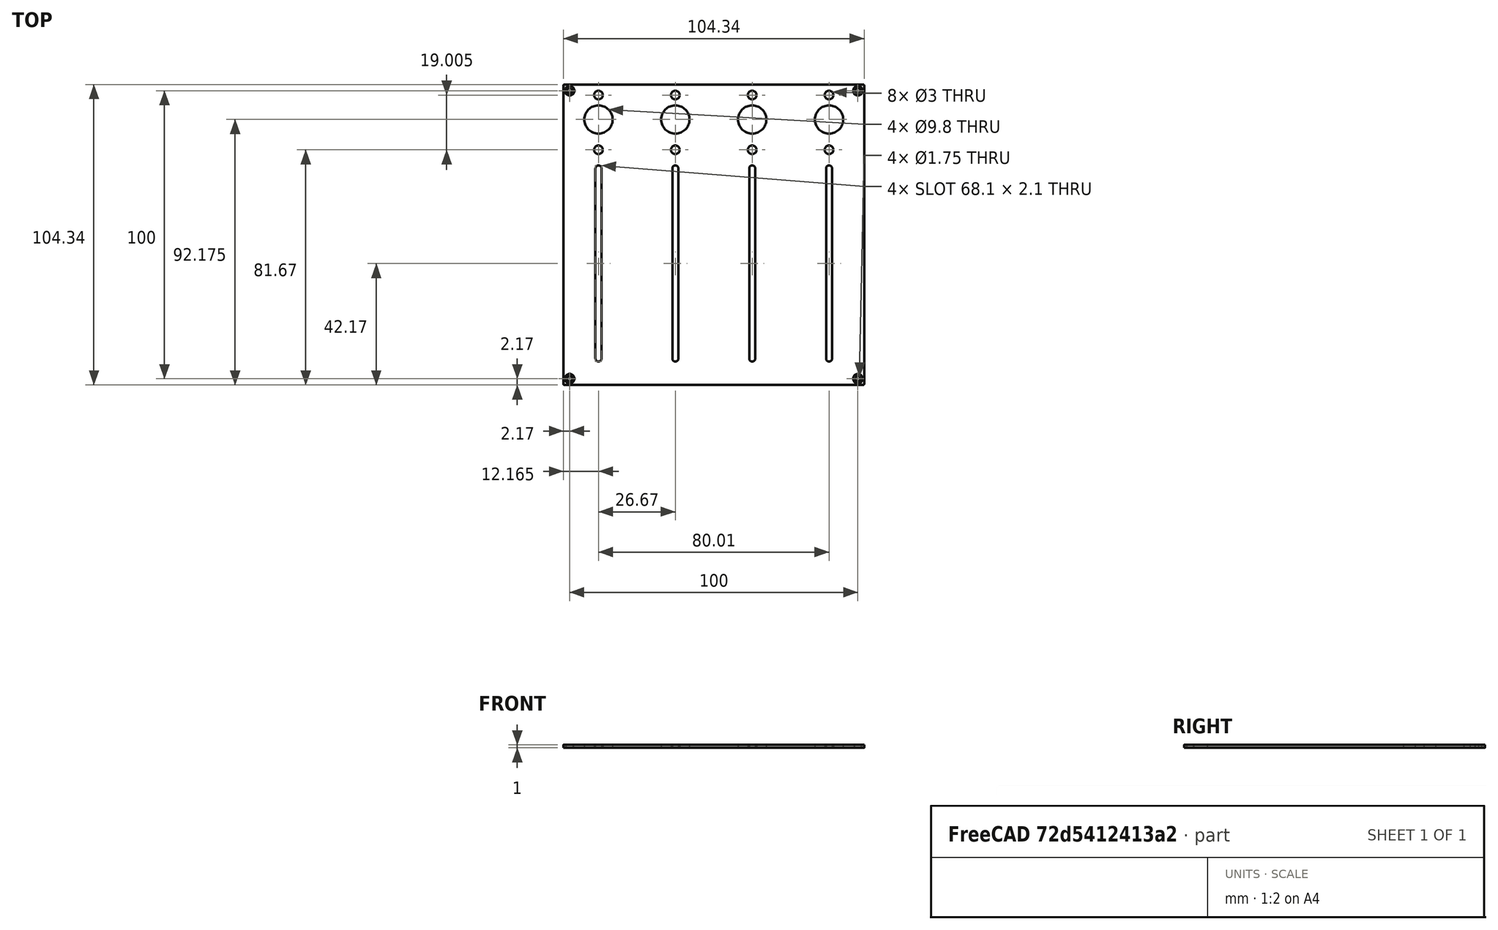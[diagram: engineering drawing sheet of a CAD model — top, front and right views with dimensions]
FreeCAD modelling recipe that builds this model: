
FCSTD DOCUMENT  (FreeCAD 0.21R33771 (Git))
Label: FRONTPANEL-SHEET-EF44
License: All rights reserved
LicenseURL: https://en.wikipedia.org/wiki/All_rights_reserved
objects: TechDraw::DrawViewBalloon×16, TechDraw::DrawViewDimension×8, Sketcher::SketchObject×7, TechDraw::DrawViewPart×5, TechDraw::DrawHatch×5, PartDesign::Hole×3, TechDraw::DrawViewAnnotation×3, TechDraw::DrawSVGTemplate×2, PartDesign::Pocket×2, PartDesign::Body×2, TechDraw::DrawPage×2, Spreadsheet::Sheet×1, PartDesign::Pad×1, PartDesign::FeatureBase×1, TechDraw::DrawComplexSection×1
note: 33 computed .brp shape members not serialized (recipe doc carries the construction recipe); baked Part::Feature solids carry a one-line shape summary decoded from their .brp

FEATURE [TechDraw::DrawSVGTemplate] Template
  EditableTexts = COLOR=Anodized matte black - RAL code: 9004; CreationDate=2024/05/14; E.G.APPROVED=APPROVED; FC-Scale=1:1; FC-Title=EF44 - frontpanel; IntechStudioLtd.=Intech Studio Ltd.; MATERIAL=Aluminum 5052-H32; REV=04; STANDARD=ISO 2768 - m
  Height = 297
  Orientation = 1
  Template = <userpath>/Desktop/A3_LandscapeTD_MODIFIED.svg
  Width = 420
FEATURE [Sketcher::SketchObject] Sketch022
  FullyConstrained = true
  MapMode = 5
  Support = -> [XY_Plane010]
  sketch-geometry (18):
    g0: Circle CenterX=-40.005 CenterY=48.505 CenterZ=0 NormalX=0 NormalY=0 NormalZ=1 AngleXU=0 Radius=2
    g1: Circle CenterX=-13.335 CenterY=48.505 CenterZ=0 NormalX=0 NormalY=0 NormalZ=1 AngleXU=0 Radius=2
    g2: Circle CenterX=13.335 CenterY=48.505 CenterZ=0 NormalX=0 NormalY=0 NormalZ=1 AngleXU=0 Radius=2
    g3: Circle CenterX=40.005 CenterY=48.505 CenterZ=0 NormalX=0 NormalY=0 NormalZ=1 AngleXU=0 Radius=2
    g4: Circle CenterX=-40.005 CenterY=29.5 CenterZ=0 NormalX=0 NormalY=0 NormalZ=1 AngleXU=0 Radius=2
    g5: Circle CenterX=-13.335 CenterY=29.5 CenterZ=0 NormalX=0 NormalY=0 NormalZ=1 AngleXU=0 Radius=2
    g6: Circle CenterX=13.335 CenterY=29.5 CenterZ=0 NormalX=0 NormalY=0 NormalZ=1 AngleXU=0 Radius=2
    g7: Circle CenterX=40.005 CenterY=29.5 CenterZ=0 NormalX=0 NormalY=0 NormalZ=1 AngleXU=0 Radius=2
    g8: LineSegment StartX=-40.005 StartY=48.505 StartZ=0 EndX=-13.335 EndY=48.505 EndZ=0
    g9: LineSegment StartX=13.335 StartY=48.505 StartZ=0 EndX=-13.335 EndY=48.505 EndZ=0
    g10: LineSegment StartX=13.335 StartY=48.505 StartZ=0 EndX=40.005 EndY=48.505 EndZ=0
    g11: LineSegment StartX=-40.005 StartY=29.5 StartZ=0 EndX=-13.335 EndY=29.5 EndZ=0
    g12: LineSegment StartX=-13.335 StartY=29.5 StartZ=0 EndX=13.335 EndY=29.5 EndZ=0
    g13: LineSegment StartX=13.335 StartY=29.5 StartZ=0 EndX=40.005 EndY=29.5 EndZ=0
    g14: LineSegment StartX=-13.335 StartY=48.505 StartZ=0 EndX=0 EndY=8.5 EndZ=0
    g15: LineSegment StartX=0 StartY=8.5 StartZ=0 EndX=13.335 EndY=48.505 EndZ=0
    g16: LineSegment StartX=-13.335 StartY=29.5 StartZ=0 EndX=0 EndY=0 EndZ=0
    g17: LineSegment StartX=0 StartY=0 StartZ=0 EndX=13.335 EndY=29.5 EndZ=0
  constraints (45):
    c: Diameter(g7) = 4
    c: Equal(g7,g6)
    c: Equal(g7,g2)
    c: Equal(g7,g3)
    c: Equal(g7,g1)
    c: Equal(g7,g5)
    c: Equal(g7,g4)
    c: Equal(g7,g0)
    c: Coincident(g8,g0)
    c: Coincident(g8,g1)
    c: Horizontal(g8)
    c: Coincident(g9,g2)
    c: Coincident(g9,g1)
    c: Horizontal(g9)
    c: Coincident(g10,g2)
    c: Coincident(g10,g3)
    c: Horizontal(g10)
    c: Coincident(g11,g4)
    c: Coincident(g11,g5)
    c: Coincident(g12,g5)
    c: Coincident(g12,g6)
    c: Horizontal(g12)
    c: Coincident(g13,g6)
    c: Coincident(g13,g7)
    c: Horizontal(g13)
    c: Horizontal(g11)
    c: Equal(g11,g12)
    c: Equal(g12,g13)
    c: Equal(g13,g10)
    c: Equal(g10,g9)
    c: Equal(g9,g8)
    c: Coincident(g14,g1)
    c: PointOnObject(g14,g-2)
    c: Coincident(g14,g15)
    c: Coincident(g15,g2)
    c: Equal(g14,g15)
    c: DistanceX(g8,g8) = 26.67
    c: DistanceY(g-1,g14) = 8.5
    c: DistanceY(g14,g1) = 40.005
    c: DistanceY(g-1,g5) = 29.5
    c: Coincident(g16,g5)
    c: Coincident(g16,g-1)
    c: Coincident(g16,g17)
    c: Coincident(g17,g6)
    c: Equal(g17,g16)
FEATURE [Spreadsheet::Sheet] Spreadsheet  label="dim"
  cells = A1='panel_length; B1(panel_length)=104.35; A2='panel_thickness; B2(panel_thickness)=1; A3='panel_radius; B3(panel_radius)==(104.35 - 103.6) / 2; A5='corner_drill_dist; B5(corner_drill_dist)=100; A6='corner_drill_dia; B6(corner_drill_dia)=1.75; A7='corner_drill_countersink; B7(corner_drill_countersink)=3.3; A9='undercut_width; B9(undercut_width)=1; A10='undercut_length; B10(undercut_length)=90; A11='undercut_offset; B11(undercut_offset)=1; A12='undercut_depth; B12(undercut_depth)=0.8; A14='ui_raster; B14(ui_raster)=26.67; A16='light_drill_dia; B16(light_drill_dia)=3; D16='old 2.9; A17='light_bore_dia; B17(light_bore_dia)=3.45; C17='check; D17='old 3.30; E17='DEPRICATED; A18='light_bore_depth; B18(light_bore_depth)=0.4; C18='check; D18='old 0.40; E18='DEPRICATED; A20='pot_drill_dia; B20(pot_drill_dia)=9.8; C20='check; D20='old 6.20; A21='pot_led_dist; B21(pot_led_dist)=8.5; B22=0; A23='but_drill_dia; B23(but_drill_dia)=9.8; A24='but_led_dist; B24(but_led_dist)=8.5; A26='fad_cutout_width; B26(fad_cutout_width)=2.1; C26='check; D26='old 1.50; A27='fad_cutout_length; B27(fad_cutout_length)=36; A28='fad_led_dist; B28(fad_led_dist)=25; A30='enc_drill_dia; B30(enc_drill_dia)=9.8; C30='check; D30='old 6.20; A31='enc_led_dist; B31(enc_led_dist)=8.5; A33='longfad_cutout_width; B33(longfad_cutout_width)=2.1; A34='longfad_cutout_length; B34(longfad_cutout_length)=66; A36='panel_chamfer; B36(panel_chamfer)=0.2; C36='UPDATE DRAWING
FEATURE [Sketcher::SketchObject] Sketch021
  FullyConstrained = true
  MapMode = 5
  Support = -> [XY_Plane010]
  expr: Constraints[48] = <<dim>>.longfad_cutout_length
  expr: Constraints[49] = <<dim>>.longfad_cutout_width
  sketch-geometry (25):
    g0: ArcOfCircle CenterX=-40.005 CenterY=23 CenterZ=0 NormalX=0 NormalY=0 NormalZ=1 AngleXU=0 Radius=1.05 StartAngle=-6.8008e-12 EndAngle=3.14159
    g1: ArcOfCircle CenterX=-40.005 CenterY=-43 CenterZ=0 NormalX=0 NormalY=0 NormalZ=1 AngleXU=0 Radius=1.05 StartAngle=3.14159 EndAngle=6.28319
    g2: LineSegment StartX=-41.055 StartY=23 StartZ=0 EndX=-41.055 EndY=-43 EndZ=0
    g3: LineSegment StartX=-38.955 StartY=23 StartZ=0 EndX=-38.955 EndY=-43 EndZ=0
    g4: ArcOfCircle CenterX=-13.335 CenterY=23 CenterZ=0 NormalX=0 NormalY=0 NormalZ=1 AngleXU=0 Radius=1.05 StartAngle=-1.8e-15 EndAngle=3.14159
    g5: ArcOfCircle CenterX=-13.335 CenterY=-43 CenterZ=0 NormalX=0 NormalY=0 NormalZ=1 AngleXU=0 Radius=1.05 StartAngle=3.14159 EndAngle=6.28319
    g6: LineSegment StartX=-14.385 StartY=23 StartZ=0 EndX=-14.385 EndY=-43 EndZ=0
    g7: LineSegment StartX=-12.285 StartY=23 StartZ=0 EndX=-12.285 EndY=-43 EndZ=0
    g8: ArcOfCircle CenterX=13.335 CenterY=23 CenterZ=0 NormalX=0 NormalY=0 NormalZ=1 AngleXU=0 Radius=1.05 StartAngle=-9e-16 EndAngle=3.14159
    g9: ArcOfCircle CenterX=13.335 CenterY=-43 CenterZ=0 NormalX=0 NormalY=0 NormalZ=1 AngleXU=0 Radius=1.05 StartAngle=3.14159 EndAngle=6.28319
    g10: LineSegment StartX=12.285 StartY=23 StartZ=0 EndX=12.285 EndY=-43 EndZ=0
    g11: LineSegment StartX=14.385 StartY=23 StartZ=0 EndX=14.385 EndY=-43 EndZ=0
    g12: ArcOfCircle CenterX=40.005 CenterY=23 CenterZ=0 NormalX=0 NormalY=0 NormalZ=1 AngleXU=0 Radius=1.05 StartAngle=-9e-16 EndAngle=3.14159
    g13: ArcOfCircle CenterX=40.005 CenterY=-43 CenterZ=0 NormalX=0 NormalY=0 NormalZ=1 AngleXU=0 Radius=1.05 StartAngle=3.14159 EndAngle=6.28319
    g14: LineSegment StartX=38.955 StartY=23 StartZ=0 EndX=38.955 EndY=-43 EndZ=0
    g15: LineSegment StartX=41.055 StartY=23 StartZ=0 EndX=41.055 EndY=-43 EndZ=0
    g16: LineSegment StartX=-40.005 StartY=23 StartZ=0 EndX=-13.335 EndY=23 EndZ=0
    g17: LineSegment StartX=-13.335 StartY=23 StartZ=0 EndX=13.335 EndY=23 EndZ=0
    g18: LineSegment StartX=13.335 StartY=23 StartZ=0 EndX=40.005 EndY=23 EndZ=0
    g19: LineSegment StartX=-40.005 StartY=-43 StartZ=0 EndX=-13.335 EndY=-43 EndZ=0
    g20: LineSegment StartX=-13.335 StartY=-43 StartZ=0 EndX=13.335 EndY=-43 EndZ=0
    g21: LineSegment StartX=13.335 StartY=-43 StartZ=0 EndX=40.005 EndY=-43 EndZ=0
    g22: LineSegment StartX=-13.335 StartY=23 StartZ=0 EndX=0 EndY=-10 EndZ=0
    g23: LineSegment StartX=0 StartY=-10 StartZ=0 EndX=13.335 EndY=23 EndZ=0
    g24: LineSegment StartX=-13.335 StartY=-43 StartZ=0 EndX=0 EndY=-10 EndZ=0
  constraints (59):
    c: Tangent(g0,g3) = 1.5708
    c: Tangent(g0,g2) = -1.5708
    c: Tangent(g2,g1) = -1.5708
    c: Tangent(g3,g1) = 1.5708
    c: Vertical(g2)
    c: Equal(g0,g1)
    c: Tangent(g4,g7) = 1.5708
    c: Tangent(g4,g6) = -1.5708
    c: Tangent(g6,g5) = -1.5708
    c: Tangent(g7,g5) = 1.5708
    c: Vertical(g6)
    c: Equal(g4,g5)
    c: Tangent(g8,g11) = 1.5708
    c: Tangent(g8,g10) = -1.5708
    c: Tangent(g10,g9) = -1.5708
    c: Tangent(g11,g9) = 1.5708
    c: Vertical(g10)
    c: Equal(g8,g9)
    c: Tangent(g12,g15) = 1.5708
    c: Tangent(g12,g14) = -1.5708
    c: Tangent(g14,g13) = -1.5708
    c: Tangent(g15,g13) = 1.5708
    c: Vertical(g14)
    c: Equal(g12,g13)
    c: Equal(g0,g4)
    c: Equal(g4,g8)
    c: Equal(g8,g12)
    c: Coincident(g16,g0)
    c: Coincident(g16,g4)
    c: Coincident(g16,g17)
    c: Coincident(g17,g8)
    c: Coincident(g17,g18)
    c: Coincident(g18,g12)
    c: Horizontal(g18)
    c: Coincident(g19,g1)
    c: Coincident(g19,g5)
    c: Coincident(g19,g20)
    c: Coincident(g20,g9)
    c: Coincident(g20,g21)
    c: Coincident(g21,g13)
    c: Horizontal(g21)
    c: Horizontal(g20)
    c: Horizontal(g19)
    c: Horizontal(g16)
    c: Horizontal(g17)
    c: Equal(g18,g17)
    c: Equal(g17,g16)
    c: DistanceX(g16,g16) = 26.67
    c: DistanceY(g2,g2) = 66
    c: DistanceX(g0,g0) = 2.1
    c: Coincident(g22,g4)
    c: PointOnObject(g22,g-2)
    c: Coincident(g22,g23)
    c: Coincident(g23,g8)
    c: Coincident(g24,g5)
    c: Coincident(g24,g22)
    c: DistanceY(g22,g-1) = 10
    c: Equal(g24,g22)
    c: Equal(g22,g23)
FEATURE [Sketcher::SketchObject] Sketch020
  FullyConstrained = true
  MapMode = 5
  Support = -> [XY_Plane010]
  sketch-geometry (9):
    g0: Circle CenterX=-40.005 CenterY=40.005 CenterZ=0 NormalX=0 NormalY=0 NormalZ=1 AngleXU=0 Radius=2
    g1: Circle CenterX=-13.335 CenterY=40.005 CenterZ=0 NormalX=0 NormalY=0 NormalZ=1 AngleXU=0 Radius=2
    g2: Circle CenterX=13.335 CenterY=40.005 CenterZ=0 NormalX=0 NormalY=0 NormalZ=1 AngleXU=0 Radius=2
    g3: Circle CenterX=40.005 CenterY=40.005 CenterZ=0 NormalX=0 NormalY=0 NormalZ=1 AngleXU=0 Radius=2
    g4: LineSegment StartX=40.005 StartY=40.005 StartZ=0 EndX=13.335 EndY=40.005 EndZ=0
    g5: LineSegment StartX=13.335 StartY=40.005 StartZ=0 EndX=-13.335 EndY=40.005 EndZ=0
    g6: LineSegment StartX=-40.005 StartY=40.005 StartZ=0 EndX=-13.335 EndY=40.005 EndZ=0
    g7: LineSegment StartX=-13.335 StartY=40.005 StartZ=0 EndX=0 EndY=0 EndZ=0
    g8: LineSegment StartX=13.335 StartY=40.005 StartZ=0 EndX=0 EndY=0 EndZ=0
  constraints (22):
    c: Coincident(g4,g2)
    c: Horizontal(g4)
    c: Coincident(g4,g5)
    c: Horizontal(g5)
    c: Coincident(g6,g0)
    c: Coincident(g6,g1)
    c: Horizontal(g6)
    c: Equal(g6,g5)
    c: Equal(g5,g4)
    c: DistanceX(g5,g5) = 26.67
    c: Coincident(g1,g5)
    c: Coincident(g7,g1)
    c: Coincident(g7,g-1)
    c: Coincident(g8,g2)
    c: Coincident(g8,g-1)
    c: Equal(g8,g7)
    c: DistanceY(g-1,g1) = 40.005
    c: Diameter(g0) = 4
    c: Equal(g0,g1)
    c: Equal(g0,g2)
    c: Equal(g0,g3)
    c: Coincident(g4,g3)
FEATURE [Sketcher::SketchObject] Sketch001
  FullyConstrained = true
  MapMode = 5
  Support = -> [XY_Plane]
  expr: Constraints[13] = <<dim>>.corner_drill_dist
  sketch-geometry (9):
    g0: LineSegment StartX=-50 StartY=50 StartZ=0 EndX=-50 EndY=-50 EndZ=0
    g1: LineSegment StartX=-50 StartY=-50 StartZ=0 EndX=50 EndY=-50 EndZ=0
    g2: LineSegment StartX=50 StartY=-50 StartZ=0 EndX=50 EndY=50 EndZ=0
    g3: LineSegment StartX=50 StartY=50 StartZ=0 EndX=-50 EndY=50 EndZ=0
    g4: Circle CenterX=0 CenterY=0 CenterZ=0 NormalX=0 NormalY=0 NormalZ=1 AngleXU=0 Radius=70.7107
    g5: Circle CenterX=-50 CenterY=50 CenterZ=0 NormalX=0 NormalY=0 NormalZ=1 AngleXU=0 Radius=0.5
    g6: Circle CenterX=50 CenterY=50 CenterZ=0 NormalX=0 NormalY=0 NormalZ=1 AngleXU=0 Radius=0.5
    g7: Circle CenterX=50 CenterY=-50 CenterZ=0 NormalX=0 NormalY=0 NormalZ=1 AngleXU=0 Radius=0.5
    g8: Circle CenterX=-50 CenterY=-50 CenterZ=0 NormalX=0 NormalY=0 NormalZ=1 AngleXU=0 Radius=0.5
  constraints (22):
    c: Coincident(g0,g1)
    c: Coincident(g1,g2)
    c: Coincident(g2,g3)
    c: Coincident(g3,g0)
    c: Equal(g0,g1)
    c: Equal(g0,g2)
    c: Equal(g0,g3)
    c: PointOnObject(g0,g4)
    c: PointOnObject(g1,g4)
    c: PointOnObject(g2,g4)
    c: PointOnObject(g3,g4)
    c: Coincident(g4,g-1)
    c: Horizontal(g3)
    c: DistanceX(g3,g3) = 100
    c: Coincident(g5,g0)
    c: Coincident(g6,g2)
    c: Coincident(g7,g1)
    c: Coincident(g8,g0)
    c: Diameter(g8) = 1
    c: Equal(g8,g7)
    c: Equal(g8,g6)
    c: Equal(g8,g5)
FEATURE [Sketcher::SketchObject] Sketch002
  AttachmentOffset = pos=(0,0,-4.8) rot=(0,0,1;0rad)
  FullyConstrained = true
  MapMode = 5
  Placement = pos=(0,0,-4.8) rot=(0,0,1;0rad)
  Support = -> [XY_Plane]
  expr: .AttachmentOffset.Base.z = -<<dim>>.undercut_depth - 4
  expr: Constraints[91] = <<dim>>.undercut_length
  expr: Constraints[92] = <<dim>>.undercut_width
  expr: Constraints[93] = <<dim>>.panel_length / 2 - <<dim>>.undercut_offset - <<dim>>.undercut_width / 2
  sketch-geometry (40):
    g0: LineSegment StartX=-45 StartY=50.175 StartZ=0 EndX=45 EndY=50.175 EndZ=0
    g1: LineSegment StartX=-45 StartY=51.175 StartZ=0 EndX=45 EndY=51.175 EndZ=0
    g2: LineSegment StartX=-50.675 StartY=45 StartZ=0 EndX=0 EndY=0 EndZ=0
    g3: LineSegment StartX=0 StartY=0 StartZ=0 EndX=-50.675 EndY=-45 EndZ=0
    g4: LineSegment StartX=0 StartY=0 StartZ=0 EndX=-45 EndY=50.675 EndZ=0
    g5: LineSegment StartX=45 StartY=50.675 StartZ=0 EndX=0 EndY=0 EndZ=0
    g6: LineSegment StartX=0 StartY=0 StartZ=0 EndX=50.675 EndY=45 EndZ=0
    g7: LineSegment StartX=50.675 StartY=-45 StartZ=0 EndX=0 EndY=0 EndZ=0
    g8: LineSegment StartX=0 StartY=0 StartZ=0 EndX=45 EndY=-50.675 EndZ=0
    g9: LineSegment StartX=0 StartY=0 StartZ=0 EndX=-45 EndY=-50.675 EndZ=0
    g10: ArcOfCircle CenterX=45 CenterY=50.675 CenterZ=0 NormalX=0 NormalY=0 NormalZ=1 AngleXU=0 Radius=0.5 StartAngle=4.71239 EndAngle=6.28319
    g11: ArcOfCircle CenterX=45 CenterY=50.675 CenterZ=0 NormalX=0 NormalY=0 NormalZ=1 AngleXU=0 Radius=0.5 StartAngle=0 EndAngle=1.5708
    g12: LineSegment StartX=45 StartY=50.675 StartZ=0 EndX=45.5 EndY=50.675 EndZ=0
    g13: ArcOfCircle CenterX=-45 CenterY=50.675 CenterZ=0 NormalX=0 NormalY=0 NormalZ=1 AngleXU=0 Radius=0.5 StartAngle=3.14159 EndAngle=4.71239
    g14: ArcOfCircle CenterX=-45 CenterY=50.675 CenterZ=0 NormalX=0 NormalY=0 NormalZ=1 AngleXU=0 Radius=0.5 StartAngle=1.5708 EndAngle=3.14159
    g15: LineSegment StartX=-45.5 StartY=50.675 StartZ=0 EndX=-45 EndY=50.675 EndZ=0
    g16: LineSegment StartX=-45 StartY=-51.175 StartZ=0 EndX=45 EndY=-51.175 EndZ=0
    g17: LineSegment StartX=-45 StartY=-50.175 StartZ=0 EndX=45 EndY=-50.175 EndZ=0
    g18: ArcOfCircle CenterX=45 CenterY=-50.675 CenterZ=0 NormalX=0 NormalY=0 NormalZ=1 AngleXU=0 Radius=0.5 StartAngle=4.71239 EndAngle=6.28319
    g19: ArcOfCircle CenterX=45 CenterY=-50.675 CenterZ=0 NormalX=0 NormalY=0 NormalZ=1 AngleXU=0 Radius=0.5 StartAngle=0 EndAngle=1.5708
    g20: LineSegment StartX=45 StartY=-50.675 StartZ=0 EndX=45.5 EndY=-50.675 EndZ=0
    g21: ArcOfCircle CenterX=-45 CenterY=-50.675 CenterZ=0 NormalX=0 NormalY=0 NormalZ=1 AngleXU=0 Radius=0.5 StartAngle=3.14159 EndAngle=4.71239
    g22: ArcOfCircle CenterX=-45 CenterY=-50.675 CenterZ=0 NormalX=0 NormalY=0 NormalZ=1 AngleXU=0 Radius=0.5 StartAngle=1.5708 EndAngle=3.14159
    g23: LineSegment StartX=-45.5 StartY=-50.675 StartZ=0 EndX=-45 EndY=-50.675 EndZ=0
    g24: LineSegment StartX=51.175 StartY=-45 StartZ=0 EndX=51.175 EndY=45 EndZ=0
    g25: LineSegment StartX=50.175 StartY=-45 StartZ=0 EndX=50.175 EndY=45 EndZ=0
    g26: ArcOfCircle CenterX=50.675 CenterY=45 CenterZ=0 NormalX=0 NormalY=0 NormalZ=1 AngleXU=0 Radius=0.5 StartAngle=3.8e-15 EndAngle=1.5708
    g27: ArcOfCircle CenterX=50.675 CenterY=45 CenterZ=0 NormalX=0 NormalY=0 NormalZ=1 AngleXU=0 Radius=0.5 StartAngle=1.5708 EndAngle=3.14159
    g28: LineSegment StartX=50.675 StartY=45 StartZ=0 EndX=50.675 EndY=45.5 EndZ=0
    g29: ArcOfCircle CenterX=50.675 CenterY=-45 CenterZ=0 NormalX=0 NormalY=0 NormalZ=1 AngleXU=0 Radius=0.5 StartAngle=4.71239 EndAngle=6.28319
    g30: ArcOfCircle CenterX=50.675 CenterY=-45 CenterZ=0 NormalX=0 NormalY=0 NormalZ=1 AngleXU=0 Radius=0.5 StartAngle=3.14159 EndAngle=4.71239
    g31: LineSegment StartX=50.675 StartY=-45.5 StartZ=0 EndX=50.675 EndY=-45 EndZ=0
    g32: LineSegment StartX=-50.175 StartY=-45 StartZ=0 EndX=-50.175 EndY=45 EndZ=0
    g33: LineSegment StartX=-51.175 StartY=-45 StartZ=0 EndX=-51.175 EndY=45 EndZ=0
    g34: ArcOfCircle CenterX=-50.675 CenterY=45 CenterZ=0 NormalX=0 NormalY=0 NormalZ=1 AngleXU=0 Radius=0.5 StartAngle=1.4e-15 EndAngle=1.5708
    g35: ArcOfCircle CenterX=-50.675 CenterY=45 CenterZ=0 NormalX=0 NormalY=0 NormalZ=1 AngleXU=0 Radius=0.5 StartAngle=1.5708 EndAngle=3.14159
    g36: LineSegment StartX=-50.675 StartY=45 StartZ=0 EndX=-50.675 EndY=45.5 EndZ=0
    g37: ArcOfCircle CenterX=-50.675 CenterY=-45 CenterZ=0 NormalX=0 NormalY=0 NormalZ=1 AngleXU=0 Radius=0.5 StartAngle=4.71239 EndAngle=6.28319
    g38: ArcOfCircle CenterX=-50.675 CenterY=-45 CenterZ=0 NormalX=0 NormalY=0 NormalZ=1 AngleXU=0 Radius=0.5 StartAngle=3.14159 EndAngle=4.71239
    g39: LineSegment StartX=-50.675 StartY=-45.5 StartZ=0 EndX=-50.675 EndY=-45 EndZ=0
  constraints (96):
    c: Horizontal(g0)
    c: Coincident(g2,g-1)
    c: Coincident(g2,g3)
    c: Coincident(g-1,g4)
    c: Coincident(g5,g-1)
    c: Coincident(g5,g6)
    c: Coincident(g7,g-1)
    c: Coincident(g7,g8)
    c: Coincident(g-1,g9)
    c: Equal(g5,g6)
    c: Equal(g6,g8)
    c: Equal(g8,g7)
    c: Equal(g7,g9)
    c: Equal(g9,g3)
    c: Equal(g3,g2)
    c: Equal(g2,g4)
    c: Coincident(g10,g5)
    c: Coincident(g11,g10)
    c: Coincident(g11,g10)
    c: Tangent(g11,g1) = 1.5708
    c: Tangent(g10,g0) = -1.5708
    c: Coincident(g12,g10)
    c: Coincident(g12,g10)
    c: Horizontal(g12)
    c: Coincident(g13,g4)
    c: Coincident(g14,g13)
    c: Coincident(g14,g13)
    c: Tangent(g14,g1) = 1.5708
    c: Tangent(g13,g0) = -1.5708
    c: Coincident(g15,g13)
    c: Coincident(g15,g13)
    c: Horizontal(g15)
    c: Horizontal(g1)
    c: Horizontal(g16)
    c: Coincident(g19,g18)
    c: Coincident(g19,g18)
    c: Tangent(g19,g17) = 1.5708
    c: Tangent(g18,g16) = -1.5708
    c: Coincident(g20,g18)
    c: Coincident(g20,g18)
    c: Horizontal(g20)
    c: Coincident(g22,g21)
    c: Coincident(g22,g21)
    c: Tangent(g22,g17) = 1.5708
    c: Tangent(g21,g16) = -1.5708
    c: Coincident(g23,g21)
    c: Coincident(g23,g21)
    c: Horizontal(g23)
    c: Horizontal(g17)
    c: Coincident(g21,g9)
    c: Coincident(g8,g18)
    c: Equal(g22,g14)
    c: Equal(g17,g1)
    c: Coincident(g27,g26)
    c: Coincident(g27,g26)
    c: Tangent(g27,g25) = 1.5708
    c: Tangent(g26,g24) = -1.5708
    c: Coincident(g28,g26)
    c: Coincident(g28,g26)
    c: Coincident(g30,g29)
    c: Coincident(g30,g29)
    c: Tangent(g30,g25) = 1.5708
    c: Tangent(g29,g24) = -1.5708
    c: Coincident(g31,g29)
    c: Coincident(g31,g29)
    c: Vertical(g31)
    c: Vertical(g28)
    c: Vertical(g25)
    c: Vertical(g24)
    c: Coincident(g35,g34)
    c: Coincident(g35,g34)
    c: Tangent(g35,g33) = 1.5708
    c: Tangent(g34,g32) = -1.5708
    c: Coincident(g36,g34)
    c: Coincident(g36,g34)
    c: Coincident(g38,g37)
    c: Coincident(g38,g37)
    c: Tangent(g38,g33) = 1.5708
    c: Tangent(g37,g32) = -1.5708
    c: Coincident(g39,g37)
    c: Coincident(g39,g37)
    c: Vertical(g39)
    c: Vertical(g36)
    c: Vertical(g33)
    c: Vertical(g32)
    c: Coincident(g6,g26)
    c: Coincident(g7,g29)
    c: Equal(g25,g0)
    c: Equal(g11,g27)
    c: Equal(g1,g33)
    c: Equal(g35,g11)
    c: DistanceX(g13,g10) = 90
    c: Diameter(g13) = 1
    c: DistanceY(g-1,g13) = 50.675
    c: Coincident(g2,g34)
    c: Coincident(g3,g37)
FEATURE [Sketcher::SketchObject] Sketch
  FullyConstrained = true
  MapMode = 5
  Support = -> [XY_Plane]
  expr: Constraints[12] = <<dim>>.panel_radius
  expr: Constraints[16] = <<dim>>.panel_length
  sketch-geometry (11):
    g0: LineSegment StartX=-51.8 StartY=52.175 StartZ=0 EndX=51.8 EndY=52.175 EndZ=0
    g1: LineSegment StartX=52.175 StartY=51.8 StartZ=0 EndX=52.175 EndY=-51.8 EndZ=0
    g2: LineSegment StartX=51.8 StartY=-52.175 StartZ=0 EndX=-51.8 EndY=-52.175 EndZ=0
    g3: LineSegment StartX=-52.175 StartY=-51.8 StartZ=0 EndX=-52.175 EndY=51.8 EndZ=0
    g4: ArcOfCircle CenterX=-51.8 CenterY=51.8 CenterZ=0 NormalX=0 NormalY=0 NormalZ=1 AngleXU=0 Radius=0.375 StartAngle=1.5708 EndAngle=3.14159
    g5: ArcOfCircle CenterX=51.8 CenterY=51.8 CenterZ=0 NormalX=0 NormalY=0 NormalZ=1 AngleXU=0 Radius=0.375 StartAngle=8.4e-15 EndAngle=1.5708
    g6: ArcOfCircle CenterX=51.8 CenterY=-51.8 CenterZ=0 NormalX=0 NormalY=0 NormalZ=1 AngleXU=0 Radius=0.375 StartAngle=4.71239 EndAngle=6.28319
    g7: ArcOfCircle CenterX=-51.8 CenterY=-51.8 CenterZ=0 NormalX=0 NormalY=0 NormalZ=1 AngleXU=0 Radius=0.375 StartAngle=3.14159 EndAngle=4.71239
    g8: LineSegment StartX=-51.8 StartY=51.8 StartZ=0 EndX=0 EndY=0 EndZ=0
    g9: LineSegment StartX=0 StartY=0 StartZ=0 EndX=51.8 EndY=51.8 EndZ=0
    g10: LineSegment StartX=0 StartY=0 StartZ=0 EndX=-51.8 EndY=-51.8 EndZ=0
  constraints (26):
    c: Horizontal(g0)
    c: Horizontal(g2)
    c: Vertical(g1)
    c: Vertical(g3)
    c: Tangent(g3,g4) = 1.5708
    c: Tangent(g0,g4) = 1.5708
    c: Tangent(g0,g5) = 1.5708
    c: Tangent(g1,g5) = 1.5708
    c: Tangent(g1,g6) = 1.5708
    c: Tangent(g2,g6) = 1.5708
    c: Tangent(g2,g7) = 1.5708
    c: Tangent(g3,g7) = 1.5708
    c: Radius(g4) = 0.375
    c: Equal(g4,g5)
    c: Equal(g4,g6)
    c: Equal(g4,g7)
    c: DistanceX(g3,g1) = 104.35
    c: Equal(g3,g0)
    c: Coincident(g8,g4)
    c: Coincident(g8,g-1)
    c: Coincident(g8,g9)
    c: Coincident(g9,g5)
    c: Coincident(g-1,g10)
    c: Coincident(g10,g7)
    c: Equal(g10,g8)
    c: Equal(g8,g9)
FEATURE [PartDesign::Pad] Pad  label="panel"
  AllowMultiFace = false
  Direction = (0,0,1)
  Length = 1
  Length2 = 100
  Profile = -> Sketch
  Reversed = true
  Type = 0
  expr: Length = <<dim>>.panel_thickness
FEATURE [PartDesign::Pocket] Pocket
  AllowMultiFace = false
  BaseFeature = -> Pad
  Direction = (0,0,-1)
  Length = 5
  Length2 = 100
  Profile = -> Sketch002
  Type = 1
FEATURE [PartDesign::Hole] Hole
  BaseFeature = -> Pocket
  CustomThreadClearance = 0
  Depth = 298.105
  DepthType = 1
  Diameter = 1.75
  DrillForDepth = false
  DrillPoint = 1
  DrillPointAngle = 118
  HoleCutCountersinkAngle = 90
  HoleCutCustomValues = false
  HoleCutDepth = 0
  HoleCutDiameter = 3.3
  HoleCutType = 2
  ModelThread = false
  Profile = -> Sketch001
  Tapered = false
  TaperedAngle = 90
  ThreadClass = 0
  ThreadDepth = 298.105
  ThreadDepthType = 0
  ThreadDirection = 0
  ThreadFit = 0
  ThreadSize = 0
  ThreadType = 0
  Threaded = false
  UseCustomThreadClearance = false
  expr: Diameter = <<dim>>.corner_drill_dia
  expr: HoleCutDiameter = <<dim>>.corner_drill_countersink
FEATURE [PartDesign::Body] Body  label="Base"
  Group = -> [Sketch,Pad,Sketch001,Sketch002,Pocket,Hole]
  Origin = -> Origin
  Tip = -> Hole
FEATURE [PartDesign::FeatureBase] Clone008
  BaseFeature = -> Body
FEATURE [PartDesign::Hole] Hole012
  BaseFeature = -> Clone008
  CustomThreadClearance = 0
  Depth = 25
  DepthType = 1
  Diameter = 9.8
  DrillForDepth = false
  DrillPoint = 1
  DrillPointAngle = 118
  HoleCutCountersinkAngle = 90
  HoleCutCustomValues = false
  HoleCutDepth = 0
  HoleCutDiameter = 6.1
  HoleCutType = 0
  ModelThread = false
  Profile = -> Sketch020
  Tapered = false
  TaperedAngle = 90
  ThreadClass = 0
  ThreadDepth = 23.5
  ThreadDepthType = 0
  ThreadDirection = 0
  ThreadFit = 0
  ThreadSize = 0
  ThreadType = 0
  Threaded = false
  UseCustomThreadClearance = false
  expr: Diameter = <<dim>>.enc_drill_dia
FEATURE [PartDesign::Pocket] Pocket006
  BaseFeature = -> Hole012
  Direction = (0,0,-1)
  Length = 5
  Length2 = 100
  Profile = -> Sketch021
  Type = 1
FEATURE [PartDesign::Hole] Hole013
  BaseFeature = -> Pocket006
  CustomThreadClearance = 0
  Depth = 298.105
  DepthType = 1
  Diameter = 3
  DrillForDepth = false
  DrillPoint = 1
  DrillPointAngle = 118
  HoleCutCountersinkAngle = 90
  HoleCutCustomValues = false
  HoleCutDepth = 0.4
  HoleCutDiameter = 3.45
  HoleCutType = 0
  ModelThread = false
  Profile = -> Sketch022
  Tapered = false
  TaperedAngle = 90
  ThreadClass = 0
  ThreadDepth = 298.105
  ThreadDepthType = 0
  ThreadDirection = 0
  ThreadFit = 0
  ThreadSize = 0
  ThreadType = 0
  Threaded = false
  UseCustomThreadClearance = false
  expr: Diameter = <<dim>>.light_drill_dia
  expr: HoleCutDepth = <<dim>>.light_bore_depth
  expr: HoleCutDiameter = <<dim>>.light_bore_dia
FEATURE [Sketcher::SketchObject] Sketch023
  ExternalGeometry = -> [Hole013]
  FullyConstrained = true
  MapMode = 5
  Support = -> [XY_Plane010]
  sketch-geometry (1):
    g0: LineSegment StartX=-53.5 StartY=-50 StartZ=0 EndX=-46.5 EndY=-50 EndZ=0
  constraints (3):
    c: Horizontal(g0)
    c: Symmetric(g0,g0,g-3)
    c: DistanceX(g0,g0) = 7
FEATURE [PartDesign::Body] Body010  label="FRONTPANEL-SHEET-EF44"
  BaseFeature = -> Body
  Group = -> [Clone008,Sketch020,Hole012,Sketch021,Pocket006,Sketch022,Hole013,Sketch023]
  Origin = -> Origin010
  Tip = -> Hole013
FEATURE [TechDraw::DrawViewPart] View
  CoarseView = false
  Direction = (0,0,1)
  Focus = 100
  HardHidden = true
  IsoCount = 0
  IsoHidden = false
  IsoVisible = false
  LockPosition = false
  Perspective = false
  Rotation = 0
  ScaleType = 0
  ScrubCount = 0
  SeamHidden = false
  SeamVisible = true
  SmoothHidden = false
  SmoothVisible = true
  Source = -> [Body010]
  X = 90.2112
  XDirection = (1,0,0)
  Y = 200.59
FEATURE [TechDraw::DrawViewPart] View001
  CoarseView = false
  Direction = (-1,0,0)
  Focus = 100
  HardHidden = true
  IsoCount = 0
  IsoHidden = false
  IsoVisible = false
  LockPosition = false
  Perspective = false
  Rotation = 0
  ScaleType = 0
  ScrubCount = 0
  SeamHidden = false
  SeamVisible = true
  SmoothHidden = false
  SmoothVisible = true
  Source = -> [Body010]
  X = 184.608
  XDirection = (0,0,1)
  Y = 207.536
FEATURE [TechDraw::DrawViewPart] View002
  CoarseView = false
  Direction = (0,0,-1)
  Focus = 100
  HardHidden = true
  IsoCount = 0
  IsoHidden = false
  IsoVisible = false
  LockPosition = false
  Perspective = false
  Rotation = 0
  ScaleType = 0
  ScrubCount = 0
  SeamHidden = false
  SeamVisible = true
  SmoothHidden = false
  SmoothVisible = true
  Source = -> [Body010]
  X = 277.677
  XDirection = (-1,0,0)
  Y = 201.259
FEATURE [TechDraw::DrawViewDimension] Dimension
  AngleOverride = false
  Arbitrary = false
  ArbitraryTolerances = false
  EqualTolerance = false
  ExtensionAngle = 0
  FormatSpec = %.2w
  FormatSpecOverTolerance = %+.2w
  FormatSpecUnderTolerance = %+.2w
  Inverted = false
  LineAngle = 0
  LockPosition = false
  MeasureType = 1
  OverTolerance = 0
  References2D = -> [View]
  Rotation = 0
  ScaleType = 0
  TheoreticalExact = false
  Type = 2
  UnderTolerance = -0.2
  X = 59.5652
  Y = 2.03258
FEATURE [TechDraw::DrawViewBalloon] Balloon
  BubbleShape = 6
  EndType = 6
  EndTypeScale = 1
  KinkLength = 0
  LockPosition = false
  OriginX = 68.4335
  OriginY = 52.2781
  Rotation = 0
  ScaleType = 0
  ShapeScale = 1
  SourceView = -> Dimension
  Text = C
  TextWrapLen = -1
  X = 68.5025
  Y = 62.8988
FEATURE [TechDraw::DrawViewBalloon] Balloon001
  BubbleShape = 1
  EndType = 0
  EndTypeScale = 1
  KinkLength = -0.1
  LockPosition = false
  OriginX = -52.0652
  OriginY = 52.0652
  Rotation = 0
  ScaleType = 0
  ShapeScale = 1
  SourceView = -> View
  Text = 4x R0,38
  TextWrapLen = -1
  X = -68.4081
  Y = 67.6137
FEATURE [TechDraw::DrawViewDimension] Dimension001
  AngleOverride = false
  Arbitrary = false
  ArbitraryTolerances = true
  EqualTolerance = false
  ExtensionAngle = 0
  FormatSpec = 4x ⌀%.2w
  FormatSpecOverTolerance = +0,15
  FormatSpecUnderTolerance = 0
  Inverted = false
  LineAngle = 0
  LockPosition = false
  MeasureType = 1
  OverTolerance = 0
  References2D = -> [View]
  Rotation = 0
  ScaleType = 0
  TheoreticalExact = false
  Type = 5
  UnderTolerance = 0
  X = -11.0547
  Y = 83.1372
FEATURE [TechDraw::DrawViewBalloon] Balloon002
  BubbleShape = 6
  EndType = 6
  EndTypeScale = 1
  KinkLength = 0
  LockPosition = false
  OriginX = -14.7848
  OriginY = 70.8989
  Rotation = 0
  ScaleType = 0
  ShapeScale = 1
  SourceView = -> Dimension001
  Text = ⌖|⌀ 0,15|A|B|C
  TextWrapLen = -1
  X = 8.68964
  Y = 70.3525
FEATURE [TechDraw::DrawViewBalloon] Balloon003
  BubbleShape = 6
  EndType = 6
  EndTypeScale = 1
  KinkLength = 0
  LockPosition = false
  OriginX = -16.4193
  OriginY = 66.1263
  Rotation = 0
  ScaleType = 0
  ShapeScale = 1
  SourceView = -> Balloon002
  Text = ○|0,1
  TextWrapLen = -1
  X = -10.3842
  Y = 59.7571
FEATURE [TechDraw::DrawViewDimension] Dimension002
  AngleOverride = false
  Arbitrary = false
  ArbitraryTolerances = false
  EqualTolerance = true
  ExtensionAngle = 0
  FormatSpec = 8x ⌀%.2w
  FormatSpecOverTolerance = %+.2w
  FormatSpecUnderTolerance = %+.2w
  Inverted = false
  LineAngle = 0
  LockPosition = false
  MeasureType = 1
  OverTolerance = 0.05
  References2D = -> [View002]
  Rotation = 0
  ScaleType = 0
  TheoreticalExact = false
  Type = 5
  UnderTolerance = -0.05
  X = 77.9142
  Y = 50.2438
FEATURE [TechDraw::DrawViewDimension] Dimension003
  AngleOverride = false
  Arbitrary = false
  ArbitraryTolerances = false
  EqualTolerance = false
  ExtensionAngle = 0
  FormatSpec = %.2w
  FormatSpecOverTolerance = %+.2w
  FormatSpecUnderTolerance = %+.2w
  Inverted = false
  LineAngle = 0
  LockPosition = false
  MeasureType = 1
  OverTolerance = 0
  References2D = -> [View002]
  Rotation = 0
  ScaleType = 0
  TheoreticalExact = false
  Type = 1
  UnderTolerance = -0.2
  X = -0.512094
  Y = 67.4695
FEATURE [TechDraw::DrawViewBalloon] Balloon004
  BubbleShape = 6
  EndType = 6
  EndTypeScale = 1
  KinkLength = -0.1
  LockPosition = false
  OriginX = -52.1894
  OriginY = 60.5046
  Rotation = 0
  ScaleType = 0
  ShapeScale = 1
  SourceView = -> Dimension003
  Text = B
  TextWrapLen = -1
  X = -62.6149
  Y = 60.5466
FEATURE [TechDraw::DrawViewBalloon] Balloon005
  BubbleShape = 6
  EndType = 6
  EndTypeScale = 1
  KinkLength = 0
  LockPosition = false
  OriginX = 69.4002
  OriginY = 40.0653
  Rotation = 0
  ScaleType = 0
  ShapeScale = 1
  SourceView = -> Dimension002
  Text = ⌖|⌀ 0,15|A|B|C
  TextWrapLen = -1
  X = 91.8068
  Y = 39.4128
FEATURE [TechDraw::DrawViewBalloon] Balloon006
  BubbleShape = 6
  EndType = 6
  EndTypeScale = 1
  KinkLength = -0.1
  LockPosition = false
  OriginX = 0.573529
  OriginY = 41.1072
  Rotation = 0
  ScaleType = 0
  ShapeScale = 1
  SourceView = -> View001
  Text = A
  TextWrapLen = -1
  X = 10.2267
  Y = 41.1896
FEATURE [TechDraw::DrawViewBalloon] Balloon007
  BubbleShape = 6
  EndType = 0
  EndTypeScale = 1
  KinkLength = -0.1
  LockPosition = false
  OriginX = 0.5
  OriginY = 0
  Rotation = 0
  ScaleType = 0
  ShapeScale = 1
  SourceView = -> View001
  Text = ⏥|0,2
  TextWrapLen = -1
  X = 18.7109
  Y = 0.125522
FEATURE [TechDraw::DrawComplexSection] ComplexSection  label="Section A - A"
  BaseView = -> View
  Caption = Section A-A
  CoarseView = false
  CutSurfaceDisplay = 3
  CuttingToolWireObject = -> Sketch023
  Direction = (1e-16,-1,0)
  FileGeomPattern = C:/Program Files/FreeCAD 0.21/data/Mod/TechDraw/PAT/FCPAT.pat
  FileHatchPattern = C:/Program Files/FreeCAD 0.21/data/Mod/TechDraw/Patterns/simple.svg
  Focus = 100
  FuseBeforeCut = false
  HardHidden = true
  HatchOffset = (0,0,0)
  HatchRotation = 0
  HatchScale = 1
  IsoCount = 0
  IsoHidden = false
  IsoVisible = false
  LockPosition = false
  NameGeomPattern = Gyémánt bevonatú
  Perspective = false
  ProjectionStrategy = 1
  Rotation = 0
  Scale = 10
  ScaleType = 2
  ScrubCount = 0
  SeamHidden = false
  SeamVisible = true
  SectionDirection = 4
  SectionNormal = (1e-16,-1,0)
  SectionOrigin = (0,0,0)
  SectionSymbol = A
  SmoothHidden = false
  SmoothVisible = true
  Source = -> [Body010]
  TrimAfterCut = false
  X = 84.1826
  XDirection = (1,1e-16,0)
  Y = 67.2566
FEATURE [TechDraw::DrawViewDimension] Dimension004
  AngleOverride = false
  Arbitrary = false
  ArbitraryTolerances = false
  EqualTolerance = true
  ExtensionAngle = 0
  FormatSpec = %.2w
  FormatSpecOverTolerance = %+.2w
  FormatSpecUnderTolerance = %+.2w
  Inverted = false
  LineAngle = 0
  LockPosition = false
  MeasureType = 1
  OverTolerance = 0
  References2D = -> [ComplexSection]
  Rotation = 0
  ScaleType = 0
  TheoreticalExact = false
  Type = 6
  UnderTolerance = 0
  X = -20.2262
  Y = 22.9317
FEATURE [TechDraw::DrawViewDimension] Dimension005
  AngleOverride = false
  Arbitrary = false
  ArbitraryTolerances = false
  EqualTolerance = true
  ExtensionAngle = 0
  FormatSpec = 4x ⌀%.2w
  FormatSpecOverTolerance = %+.2w
  FormatSpecUnderTolerance = %+.2w
  Inverted = false
  LineAngle = 0
  LockPosition = false
  MeasureType = 1
  OverTolerance = 0
  References2D = -> [ComplexSection]
  Rotation = 0
  ScaleType = 0
  TheoreticalExact = false
  Type = 1
  UnderTolerance = 0
  X = 27.3597
  Y = 16.4075
FEATURE [TechDraw::DrawViewDimension] Dimension006
  AngleOverride = false
  Arbitrary = false
  ArbitraryTolerances = false
  EqualTolerance = true
  ExtensionAngle = 0
  FormatSpec = 4x ⌀%.2w
  FormatSpecOverTolerance = %+.2w
  FormatSpecUnderTolerance = %+.2w
  Inverted = false
  LineAngle = 0
  LockPosition = false
  MeasureType = 1
  OverTolerance = 0.05
  References2D = -> [ComplexSection]
  Rotation = 0
  ScaleType = 0
  TheoreticalExact = false
  Type = 1
  UnderTolerance = -0.05
  X = 54.7191
  Y = -4.5023
FEATURE [TechDraw::DrawViewBalloon] Balloon008
  BubbleShape = 6
  EndType = 6
  EndTypeScale = 1
  KinkLength = 0
  LockPosition = false
  OriginX = 48.9002
  OriginY = -14.6204
  Rotation = 0
  ScaleType = 0
  ShapeScale = 1
  SourceView = -> Dimension006
  Text = ⌖|⌀ 0,15|A|B|C
  TextWrapLen = -1
  X = 66.6564
  Y = -15.3087
FEATURE [TechDraw::DrawViewBalloon] Balloon010
  BubbleShape = 1
  EndType = 6
  EndTypeScale = 1
  KinkLength = 0
  LockPosition = false
  OriginX = -82.5189
  OriginY = -77.9964
  Rotation = 0
  ScaleType = 0
  ShapeScale = 1
  Text = 4x 2,1×68,1
  TextWrapLen = -1
  X = 112.945
  Y = 135.356
FEATURE [TechDraw::DrawViewPart] View003
  CoarseView = false
  Direction = (0.57735,0.57735,0.57735)
  Focus = 100
  HardHidden = true
  IsoCount = 0
  IsoHidden = false
  IsoVisible = false
  LockPosition = false
  Perspective = false
  Rotation = 0
  Scale = 0.5
  ScaleType = 2
  ScrubCount = 0
  SeamHidden = false
  SeamVisible = true
  SmoothHidden = false
  SmoothVisible = true
  Source = -> [Body010]
  X = 377.288
  XDirection = (0.707107,0,-0.707107)
  Y = 137.106
FEATURE [TechDraw::DrawHatch] Hatch  label="HatchF1"
  HatchPattern = C:/Program Files/FreeCAD 0.21/data/Mod/TechDraw/Patterns/solid.svg
  Source = -> View003 [Face1]
FEATURE [TechDraw::DrawViewBalloon] Balloon011
  BubbleShape = 1
  EndType = 3
  EndTypeScale = 1
  KinkLength = -0.1
  LockPosition = false
  OriginX = 0.205195
  OriginY = -22.3826
  Rotation = 0
  ScaleType = 0
  ShapeScale = 1
  SourceView = -> View003
  TextWrapLen = -1
  X = -89.9313
  Y = -70.6287
FEATURE [TechDraw::DrawViewAnnotation] Annotation
  Font = osifont
  LineSpace = 100
  LockPosition = false
  MaxWidth = -1
  Rotation = 0
  ScaleType = 0
  Text = 10:1
  TextSize = 4
  TextStyle = 0
  X = 84.1967
  Y = 46.4162
FEATURE [TechDraw::DrawViewAnnotation] Annotation001
  Font = osifont
  LineSpace = 100
  LockPosition = false
  MaxWidth = -1
  Rotation = 0
  ScaleType = 0
  Text = 1:2
  TextSize = 4
  TextStyle = 0
  X = 378.873
  Y = 100.095
FEATURE [TechDraw::DrawViewAnnotation] Annotation002
  Font = osifont
  LineSpace = 100
  LockPosition = false
  MaxWidth = -1
  Rotation = 0
  ScaleType = 0
  Text = The mid of the datum plane A is preferred to be near | to the lower limit of the flatness tolerance zone. | It can be achieved with an additional bending step. | Aesthetical surfaces colored red on the view | No scratches, burrs or any kind of damage allowed! | Functional surfaces colored blue on the view (all which perpendicular to the aesthetical) | No burrs or other protruding material allowed!
  TextSize = 3
  TextStyle = 0
  X = 297.441
  Y = 100.804
FEATURE [TechDraw::DrawViewBalloon] Balloon012
  BubbleShape = 2
  EndType = 6
  EndTypeScale = 1
  KinkLength = 0
  LockPosition = false
  OriginX = -101.292
  OriginY = -70.9562
  Rotation = 0
  ScaleType = 0
  ShapeScale = 1
  SourceView = -> Balloon010
  Text = 4
  TextWrapLen = -1
  X = 128.555
  Y = 107.636
FEATURE [TechDraw::DrawViewBalloon] Balloon013
  BubbleShape = 2
  EndType = 6
  EndTypeScale = 1
  KinkLength = 0
  LockPosition = false
  OriginX = -0.207813
  OriginY = 82.049
  Rotation = 0
  ScaleType = 0
  ShapeScale = 1
  SourceView = -> Dimension001
  Text = 4
  TextWrapLen = -1
  X = -32.3291
  Y = 77.365
FEATURE [TechDraw::DrawViewBalloon] Balloon014
  BubbleShape = 2
  EndType = 6
  EndTypeScale = 1
  KinkLength = 0
  LockPosition = false
  OriginX = -100.48
  OriginY = -7.88502
  Rotation = 0
  ScaleType = 0
  ShapeScale = 1
  SourceView = -> Annotation002
  Text = 4
  TextWrapLen = -1
  X = -95.5138
  Y = -2.15724
FEATURE [TechDraw::DrawViewBalloon] Balloon016
  BubbleShape = 1
  EndType = 0
  EndTypeScale = 1
  KinkLength = 0
  LockPosition = false
  OriginX = 0.661182
  OriginY = -40.7069
  Rotation = 0
  ScaleType = 0
  ShapeScale = 1
  SourceView = -> View001
  TextWrapLen = -1
  X = 31.1152
  Y = -74.1386
FEATURE [TechDraw::DrawViewDimension] Dimension009
  AngleOverride = false
  Arbitrary = false
  ArbitraryTolerances = false
  EqualTolerance = true
  ExtensionAngle = 0
  FormatSpec = 4× 2×R%.2w
  FormatSpecOverTolerance = %+.2w
  FormatSpecUnderTolerance = %+.2w
  Inverted = false
  LineAngle = 0
  LockPosition = false
  MeasureType = 1
  OverTolerance = 0
  References2D = -> [View]
  Rotation = 0
  ScaleType = 0
  TheoreticalExact = false
  Type = 4
  UnderTolerance = 0
  X = 14.3867
  Y = -89.7846
FEATURE [TechDraw::DrawViewBalloon] Balloon017
  BubbleShape = 6
  EndType = 0
  EndTypeScale = 1
  KinkLength = 7
  LockPosition = false
  OriginX = -12.285
  OriginY = -10
  Rotation = 0
  ScaleType = 0
  ShapeScale = 1
  SourceView = -> View
  Text = ⌓|0,2|A|B|C
  TextWrapLen = -1
  X = 36.2703
  Y = -75.666
FEATURE [TechDraw::DrawPage] Page  label="EF44_Drawing"
  KeepUpdated = true
  NextBalloonIndex = 26
  ProjectionType = 0
  Template = -> Template
  Views = -> [View,View001,View002,Dimension,Balloon,Balloon001,Dimension001,Balloon002,Balloon003,Dimension002,Dimension003,Balloon004,Balloon005,Balloon006,Balloon007,ComplexSection,Dimension004,Dimension005,Dimension006,Balloon008,Balloon010,View003,Balloon011,Annotation,Annotation001,Annotation002,Balloon012,Balloon013,Balloon014,Balloon016,Dimension009,Balloon017]
FEATURE [TechDraw::DrawHatch] Hatch007  label="Hatch007F40"
  HatchPattern = C:/Program Files/FreeCAD 0.21/data/Mod/TechDraw/Patterns/solid.svg
  Source = -> View003 [Face40,Face51,Face49,Face48,Face47,Face43,Face27,Face25,Face24,Face26,Face50,Face46,Face45,Face44]
FEATURE [TechDraw::DrawHatch] Hatch008  label="Hatch008F7"
  HatchPattern = C:/Program Files/FreeCAD 0.21/data/Mod/TechDraw/Patterns/solid.svg
  Source = -> View003 [Face7,Face68,Face6]
FEATURE [TechDraw::DrawHatch] Hatch009  label="Hatch009F42"
  HatchPattern = C:/Program Files/FreeCAD 0.21/data/Mod/TechDraw/Patterns/solid.svg
  Source = -> View003 [Face42,Face17,Face60,Face19,Face61,Face18,Face62,Face16,Face63]
FEATURE [TechDraw::DrawHatch] Hatch010  label="Hatch010F41"
  HatchPattern = C:/Program Files/FreeCAD 0.21/data/Mod/TechDraw/Patterns/solid.svg
  Source = -> View003 [Face41]
FEATURE [TechDraw::DrawSVGTemplate] Template001
  Height = 210
  Orientation = 1
  Template = C:/Program Files/FreeCAD 0.21/data/Mod/TechDraw/Templates/A4_Landscape_blank.svg
  Width = 297
FEATURE [TechDraw::DrawViewPart] View004
  CoarseView = false
  Direction = (0,0,1)
  Focus = 100
  HardHidden = false
  IsoCount = 0
  IsoHidden = false
  IsoVisible = true
  LockPosition = false
  Perspective = false
  Rotation = 0
  ScaleType = 0
  ScrubCount = 0
  SeamHidden = false
  SeamVisible = true
  SmoothHidden = false
  SmoothVisible = true
  Source = -> [Body010]
  X = 148.5
  XDirection = (1,0,0)
  Y = 105
FEATURE [TechDraw::DrawPage] Page001  label="EF44_dxf"
  KeepUpdated = true
  NextBalloonIndex = 1
  ProjectionType = 0
  Template = -> Template001
  Views = -> [View004]
